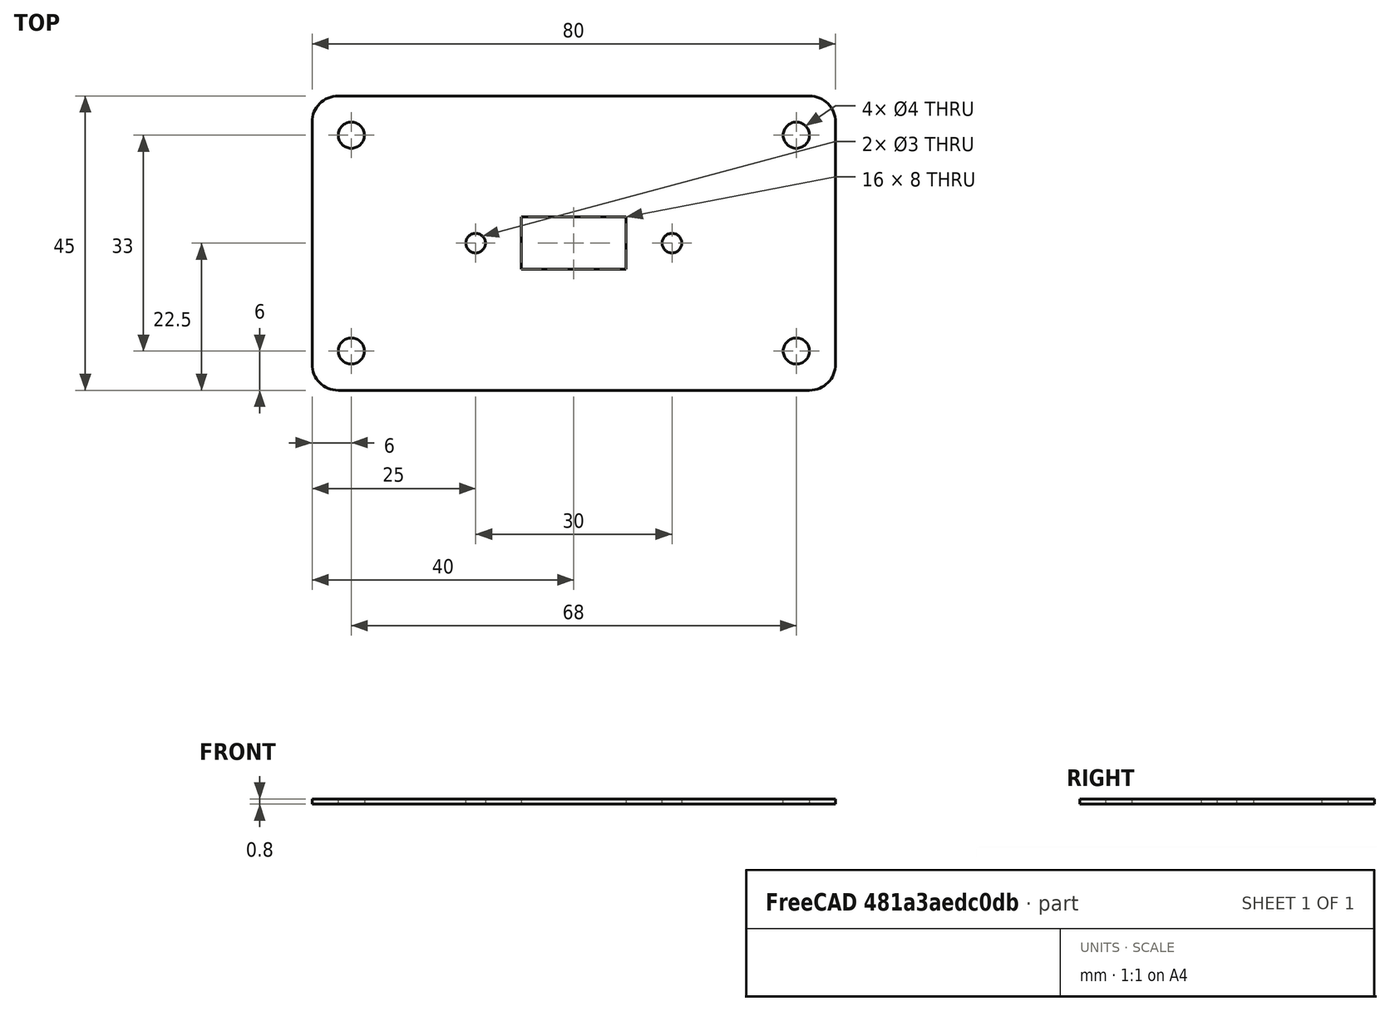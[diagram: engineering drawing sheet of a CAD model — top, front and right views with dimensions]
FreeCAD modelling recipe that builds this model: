
FCSTD DOCUMENT  (FreeCAD 0.20R29603 (Git))
Label: support-usb-pedalier-panneau-arriere
License: Public Domain
LicenseURL: http://en.wikipedia.org/wiki/Public_domain
objects: TechDraw::DrawViewDimension×12, Sketcher::SketchObject×4, PartDesign::Pocket×3, PartDesign::Pad×1, PartDesign::Body×1, TechDraw::DrawSVGTemplate×1, TechDraw::DrawViewPart×1, TechDraw::DrawPage×1
note: 13 computed .brp shape members not serialized (recipe doc carries the construction recipe); baked Part::Feature solids carry a one-line shape summary decoded from their .brp

FEATURE [Sketcher::SketchObject] Sketch
  FullyConstrained = true
  MapMode = 5
  Support = -> [XY_Plane]
  sketch-geometry (10):
    g0: ArcOfCircle CenterX=4 CenterY=41 CenterZ=0 NormalX=0 NormalY=0 NormalZ=1 AngleXU=0 Radius=4 StartAngle=1.5708 EndAngle=3.14159
    g1: LineSegment StartX=4 StartY=45 StartZ=0 EndX=76 EndY=45 EndZ=0
    g2: ArcOfCircle CenterX=76 CenterY=41 CenterZ=0 NormalX=0 NormalY=0 NormalZ=1 AngleXU=0 Radius=4 StartAngle=-9e-16 EndAngle=1.5708
    g3: LineSegment StartX=80 StartY=41 StartZ=0 EndX=80 EndY=4 EndZ=0
    g4: ArcOfCircle CenterX=76 CenterY=4 CenterZ=0 NormalX=0 NormalY=0 NormalZ=1 AngleXU=0 Radius=4 StartAngle=4.71239 EndAngle=6.28319
    g5: LineSegment StartX=76 StartY=0 StartZ=0 EndX=4 EndY=0 EndZ=0
    g6: ArcOfCircle CenterX=4 CenterY=4 CenterZ=0 NormalX=0 NormalY=0 NormalZ=1 AngleXU=0 Radius=4 StartAngle=3.14159 EndAngle=4.71239
    g7: LineSegment StartX=0 StartY=4 StartZ=0 EndX=0 EndY=41 EndZ=0
    g8: GeomPoint X=0 Y=45 Z=0
    g9: GeomPoint X=80 Y=0 Z=0
  constraints (24):
    c: Tangent(g0,g1) = 1.5708
    c: Tangent(g1,g2) = 1.5708
    c: Tangent(g2,g3) = 1.5708
    c: Tangent(g3,g4) = 1.5708
    c: Tangent(g4,g5) = 1.5708
    c: Tangent(g5,g6) = 1.5708
    c: Tangent(g6,g7) = 1.5708
    c: Tangent(g7,g0) = 1.5708
    c: Horizontal(g1)
    c: Horizontal(g5)
    c: Vertical(g3)
    c: Vertical(g7)
    c: Equal(g0,g2)
    c: Equal(g2,g4)
    c: Equal(g4,g6)
    c: PointOnObject(g8,g1)
    c: PointOnObject(g8,g7)
    c: PointOnObject(g9,g3)
    c: PointOnObject(g9,g5)
    c: DistanceX(g0,g2) = 80
    c: DistanceY(g4,g1) = 45
    c: Radius(g0) = 4
    c: PointOnObject(g0,g-2)
    c: PointOnObject(g5,g-1)
FEATURE [PartDesign::Pad] Pad
  Direction = (0,0,1)
  Length = 0.8
  Length2 = 10
  Profile = -> Sketch
  ReferenceAxis = -> Sketch [N_Axis]
  Type = 0
FEATURE [Sketcher::SketchObject] Sketch001
  ExternalGeometry = -> [Pad]
  FullyConstrained = true
  MapMode = 5
  Placement = pos=(0,0,0.8) rot=(0,0,1;0rad)
  Support = -> [Pad]
  sketch-geometry (5):
    g0: LineSegment StartX=32 StartY=26.5 StartZ=0 EndX=32 EndY=18.5 EndZ=0
    g1: LineSegment StartX=32 StartY=18.5 StartZ=0 EndX=48 EndY=18.5 EndZ=0
    g2: LineSegment StartX=48 StartY=18.5 StartZ=0 EndX=48 EndY=26.5 EndZ=0
    g3: LineSegment StartX=48 StartY=26.5 StartZ=0 EndX=32 EndY=26.5 EndZ=0
    g4: GeomPoint X=40 Y=22.5 Z=0
  constraints (12):
    c: Coincident(g0,g1)
    c: Coincident(g1,g2)
    c: Coincident(g2,g3)
    c: Coincident(g3,g0)
    c: Horizontal(g1)
    c: Horizontal(g3)
    c: Vertical(g0)
    c: Vertical(g2)
    c: Symmetric(g1,g0,g4)
    c: Symmetric(g-6,g-5,g4)
    c: DistanceX(g3,g3) = 16
    c: DistanceY(g2,g2) = 8
FEATURE [PartDesign::Pocket] Pocket
  BaseFeature = -> Pad
  Direction = (0,0,-1)
  Length = 5
  Length2 = 5
  Profile = -> Sketch001
  ReferenceAxis = -> Sketch001 [N_Axis]
  Type = 1
FEATURE [Sketcher::SketchObject] Sketch002
  ExternalGeometry = -> [Pocket]
  FullyConstrained = true
  MapMode = 5
  Placement = pos=(0,0,0.8) rot=(0,0,1;0rad)
  Support = -> [Pocket]
  sketch-geometry (5):
    g0: Circle CenterX=55 CenterY=22.5 CenterZ=0 NormalX=0 NormalY=0 NormalZ=1 AngleXU=0 Radius=1.5
    g1: Circle CenterX=25 CenterY=22.5 CenterZ=0 NormalX=0 NormalY=0 NormalZ=1 AngleXU=0 Radius=1.5
    g2: LineSegment StartX=32 StartY=18.5 StartZ=0 EndX=48 EndY=26.5 EndZ=0
    g3: LineSegment StartX=32 StartY=26.5 StartZ=0 EndX=48 EndY=18.5 EndZ=0
    g4: GeomPoint X=40 Y=22.5 Z=0
  constraints (11):
    c: Diameter(g1) = 3
    c: Diameter(g0) = 3
    c: Horizontal(g1,g0)
    c: DistanceX(g1,g0) = 30
    c: Coincident(g2,g-4)
    c: Coincident(g2,g-3)
    c: Coincident(g3,g-5)
    c: Coincident(g3,g-6)
    c: PointOnObject(g4,g2)
    c: PointOnObject(g4,g3)
    c: Symmetric(g1,g0,g4)
FEATURE [PartDesign::Pocket] Pocket001
  BaseFeature = -> Pocket
  Direction = (0,0,-1)
  Length = 5
  Length2 = 5
  Profile = -> Sketch002
  ReferenceAxis = -> Sketch002 [N_Axis]
  Type = 1
FEATURE [Sketcher::SketchObject] Sketch003
  ExternalGeometry = -> [Pocket001]
  FullyConstrained = true
  MapMode = 5
  Placement = pos=(0,0,0.8) rot=(0,0,1;0rad)
  Support = -> [Pocket001]
  sketch-geometry (4):
    g0: Circle CenterX=6 CenterY=39 CenterZ=0 NormalX=0 NormalY=0 NormalZ=1 AngleXU=0 Radius=2
    g1: Circle CenterX=74 CenterY=39 CenterZ=0 NormalX=0 NormalY=0 NormalZ=1 AngleXU=0 Radius=2
    g2: Circle CenterX=74 CenterY=6 CenterZ=0 NormalX=0 NormalY=0 NormalZ=1 AngleXU=0 Radius=2
    g3: Circle CenterX=6 CenterY=6 CenterZ=0 NormalX=0 NormalY=0 NormalZ=1 AngleXU=0 Radius=2
  constraints (12):
    c: Diameter(g0) = 4
    c: DistanceX(g-1,g0) = 6
    c: DistanceY(g0,g-3) = 6
    c: Diameter(g1) = 4
    c: Diameter(g2) = 4
    c: Diameter(g3) = 4
    c: DistanceY(g1,g-3) = 6
    c: DistanceY(g-1,g2) = 6
    c: DistanceY(g-1,g3) = 6
    c: DistanceX(g-1,g3) = 6
    c: DistanceX(g1,g-4) = 6
    c: DistanceX(g2,g-4) = 6
FEATURE [PartDesign::Pocket] Pocket002
  BaseFeature = -> Pocket001
  Direction = (0,0,-1)
  Length = 5
  Length2 = 5
  Profile = -> Sketch003
  ReferenceAxis = -> Sketch003 [N_Axis]
  Type = 1
FEATURE [PartDesign::Body] Body
  Group = -> [Sketch,Pad,Sketch001,Pocket,Sketch002,Pocket001,Sketch003,Pocket002]
  Origin = -> Origin
  Tip = -> Pocket002
FEATURE [TechDraw::DrawSVGTemplate] Template
  Height = 210
  Orientation = 1
  Width = 297
FEATURE [TechDraw::DrawViewPart] View
  CoarseView = false
  Direction = (0,0,1)
  Focus = 100
  HardHidden = false
  IsoCount = 0
  IsoHidden = false
  IsoVisible = false
  LockPosition = false
  Perspective = false
  Rotation = 0
  ScaleType = 0
  SeamHidden = false
  SeamVisible = false
  SmoothHidden = false
  SmoothVisible = false
  Source = -> [Pocket002]
  X = 148.5
  XDirection = (1,0,0)
  Y = 105
FEATURE [TechDraw::DrawViewDimension] Dimension
  AngleOverride = false
  Arbitrary = false
  ArbitraryTolerances = false
  EqualTolerance = true
  ExtensionAngle = 0
  FormatSpec = %.2w
  FormatSpecOverTolerance = %+.2w
  FormatSpecUnderTolerance = %+.2w
  Inverted = false
  LineAngle = 0
  LockPosition = false
  MeasureType = 1
  OverTolerance = 0
  References2D = -> [View]
  Rotation = 0
  ScaleType = 0
  TheoreticalExact = false
  Type = 1
  UnderTolerance = 0
  X = -19.1621
  Y = 21.4598
FEATURE [TechDraw::DrawViewDimension] Dimension001
  AngleOverride = false
  Arbitrary = false
  ArbitraryTolerances = false
  EqualTolerance = true
  ExtensionAngle = 0
  FormatSpec = %.2w
  FormatSpecOverTolerance = %+.2w
  FormatSpecUnderTolerance = %+.2w
  Inverted = false
  LineAngle = 0
  LockPosition = false
  MeasureType = 1
  OverTolerance = 0
  References2D = -> [View]
  Rotation = 0
  ScaleType = 0
  TheoreticalExact = false
  Type = 1
  UnderTolerance = 0
  X = 0.840441
  Y = 46.8856
FEATURE [TechDraw::DrawViewDimension] Dimension002
  AngleOverride = false
  Arbitrary = false
  ArbitraryTolerances = false
  EqualTolerance = true
  ExtensionAngle = 0
  FormatSpec = %.2w
  FormatSpecOverTolerance = %+.2w
  FormatSpecUnderTolerance = %+.2w
  Inverted = false
  LineAngle = 0
  LockPosition = false
  MeasureType = 1
  OverTolerance = 0
  References2D = -> [View]
  Rotation = 0
  ScaleType = 0
  TheoreticalExact = false
  Type = 2
  UnderTolerance = 0
  X = 70.7943
  Y = 2.5
FEATURE [TechDraw::DrawViewDimension] Dimension003
  AngleOverride = false
  Arbitrary = false
  ArbitraryTolerances = false
  EqualTolerance = true
  ExtensionAngle = 0
  FormatSpec = %.2w
  FormatSpecOverTolerance = %+.2w
  FormatSpecUnderTolerance = %+.2w
  Inverted = false
  LineAngle = 0
  LockPosition = false
  MeasureType = 1
  OverTolerance = 0
  References2D = -> [View]
  Rotation = 0
  ScaleType = 0
  TheoreticalExact = false
  Type = 2
  UnderTolerance = 0
  X = 8.33618
  Y = -12.2918
FEATURE [TechDraw::DrawViewDimension] Dimension004
  AngleOverride = false
  Arbitrary = false
  ArbitraryTolerances = false
  EqualTolerance = true
  ExtensionAngle = 0
  FormatSpec = %.2w
  FormatSpecOverTolerance = %+.2w
  FormatSpecUnderTolerance = %+.2w
  Inverted = false
  LineAngle = 0
  LockPosition = false
  MeasureType = 1
  OverTolerance = 0
  References2D = -> [View]
  Rotation = 0
  ScaleType = 0
  TheoreticalExact = false
  Type = 2
  UnderTolerance = 0
  X = -28.2193
  Y = -35.1228
FEATURE [TechDraw::DrawViewDimension] Dimension005
  AngleOverride = false
  Arbitrary = false
  ArbitraryTolerances = false
  EqualTolerance = true
  ExtensionAngle = 0
  FormatSpec = %.2w
  FormatSpecOverTolerance = %+.2w
  FormatSpecUnderTolerance = %+.2w
  Inverted = false
  LineAngle = 0
  LockPosition = false
  MeasureType = 1
  OverTolerance = 0
  References2D = -> [View]
  Rotation = 0
  ScaleType = 0
  TheoreticalExact = false
  Type = 1
  UnderTolerance = 0
  X = -53.2474
  Y = -4.21162
FEATURE [TechDraw::DrawViewDimension] Dimension006
  AngleOverride = false
  Arbitrary = false
  ArbitraryTolerances = false
  EqualTolerance = true
  ExtensionAngle = 0
  FormatSpec = ⌀%.2w
  FormatSpecOverTolerance = %+.2w
  FormatSpecUnderTolerance = %+.2w
  Inverted = false
  LineAngle = 0
  LockPosition = false
  MeasureType = 1
  OverTolerance = 0
  References2D = -> [View]
  Rotation = 0
  ScaleType = 0
  TheoreticalExact = false
  Type = 5
  UnderTolerance = 0
  X = -19.6663
  Y = 12.6066
FEATURE [TechDraw::DrawViewDimension] Dimension007
  AngleOverride = false
  Arbitrary = false
  ArbitraryTolerances = false
  EqualTolerance = true
  ExtensionAngle = 0
  FormatSpec = ⌀%.2w
  FormatSpecOverTolerance = %+.2w
  FormatSpecUnderTolerance = %+.2w
  Inverted = false
  LineAngle = 0
  LockPosition = false
  MeasureType = 1
  OverTolerance = 0
  References2D = -> [View]
  Rotation = 0
  ScaleType = 0
  TheoreticalExact = false
  Type = 5
  UnderTolerance = 0
  X = -47.0647
  Y = 12.9428
FEATURE [TechDraw::DrawViewDimension] Dimension008
  AngleOverride = false
  Arbitrary = false
  ArbitraryTolerances = false
  EqualTolerance = true
  ExtensionAngle = 0
  FormatSpec = %.2w
  FormatSpecOverTolerance = %+.2w
  FormatSpecUnderTolerance = %+.2w
  Inverted = false
  LineAngle = 0
  LockPosition = false
  MeasureType = 1
  OverTolerance = 0
  References2D = -> [View]
  Rotation = 0
  ScaleType = 0
  TheoreticalExact = false
  Type = 1
  UnderTolerance = 0
  X = 27.5
  Y = -6.75
FEATURE [TechDraw::DrawViewDimension] Dimension009
  AngleOverride = false
  Arbitrary = false
  ArbitraryTolerances = false
  EqualTolerance = true
  ExtensionAngle = 0
  FormatSpec = %.2w
  FormatSpecOverTolerance = %+.2w
  FormatSpecUnderTolerance = %+.2w
  Inverted = false
  LineAngle = 0
  LockPosition = false
  MeasureType = 1
  OverTolerance = 0
  References2D = -> [View]
  Rotation = 0
  ScaleType = 0
  TheoreticalExact = false
  Type = 2
  UnderTolerance = 0
  X = 25.5
  Y = 13.75
FEATURE [TechDraw::DrawViewDimension] Dimension010
  AngleOverride = false
  Arbitrary = false
  ArbitraryTolerances = false
  EqualTolerance = true
  ExtensionAngle = 0
  FormatSpec = %.2w
  FormatSpecOverTolerance = %+.2w
  FormatSpecUnderTolerance = %+.2w
  Inverted = false
  LineAngle = 0
  LockPosition = false
  MeasureType = 1
  OverTolerance = 0
  References2D = -> [View]
  Rotation = 0
  ScaleType = 0
  TheoreticalExact = false
  Type = 1
  UnderTolerance = 0
  X = -55.0449
  Y = -20.7081
FEATURE [TechDraw::DrawViewDimension] Dimension011
  AngleOverride = false
  Arbitrary = false
  ArbitraryTolerances = false
  EqualTolerance = true
  ExtensionAngle = 0
  FormatSpec = %.2w
  FormatSpecOverTolerance = %+.2w
  FormatSpecUnderTolerance = %+.2w
  Inverted = false
  LineAngle = 0
  LockPosition = false
  MeasureType = 1
  OverTolerance = 0
  References2D = -> [View]
  Rotation = 0
  ScaleType = 0
  TheoreticalExact = false
  Type = 2
  UnderTolerance = 0
  X = 44.759
  Y = -27.1272
FEATURE [TechDraw::DrawPage] Page
  KeepUpdated = true
  NextBalloonIndex = 1
  ProjectionType = 0
  Template = -> Template
  Views = -> [View,Dimension,Dimension001,Dimension002,Dimension003,Dimension004,Dimension005,Dimension006,Dimension007,Dimension008,Dimension009,Dimension010,Dimension011]
